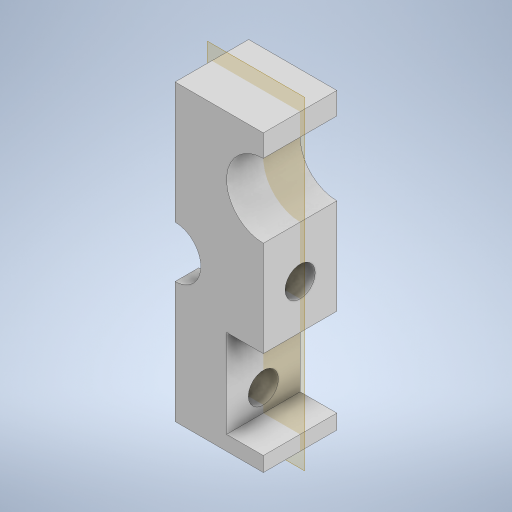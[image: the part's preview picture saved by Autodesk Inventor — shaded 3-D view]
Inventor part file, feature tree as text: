
AUTODESK INVENTOR PART (.ipt)
format: ipt  version: 2023 (Build 270158000, 158)  size: 332,288 bytes
history: native  units: mm
features: extrude x7, sketch x7, plane x1
ambient origin geometry x8: Origin, YZ Plane, XZ Plane, XY Plane, X Axis, Y Axis, Z Axis, Center Point
bodies: Solid1 (feature_tree)
feature tree (15):
  extrude  "Extrusion1"  Depth=20.0mm
  plane  "Work Plane1"
  extrude  "Extrusion2"  Depth=2.0mm
  extrude  "Extrusion3"  Depth=4.0mm
  extrude  "Extrusion4"  Depth=5.0mm TaperAngle=0.0deg
  extrude  "Extrusion5"  Depth=5.0mm TaperAngle=0.0deg
  extrude  "Extrusion6"  Depth=8.0mm TaperAngle=0.0deg
  extrude  "Extrusion7"  Depth=10.0mm
  sketch  "Sketch1"  dims[d0=20.0mm d1=20.0mm]
  sketch  "Sketch2"  dims[d2=4.0mm d6=2.0mm]
  sketch  "Sketch3"  dims[d7=2.0mm d8=4.0mm]
  sketch  "Sketch4"  dims[d9=2.0mm d10=5.0mm d11=0.0mm]
  sketch  "Sketch5"  dims[d12=5.0mm d13=1.8mm d14=0.0mm]
  sketch  "Sketch6"  dims[d15=3.5mm d16=8.0mm d17=0.0mm]
  sketch  "Sketch7"  dims[d18=2.05mm d19=2.05mm d20=2.5mm d21=2.5mm d22=2.5mm d23=2.5mm d24=5.0mm d25=0.0mm d30=5.0mm d31=0.0mm d32=2.5mm d33=1.0mm d34=6.0mm d35=5.0mm d36=4.0mm d37=5.0mm d38=0.0mm d39=2.5mm d40=10.0mm d41=2.05mm d42=12.0mm d43=0.0mm d44=6.0mm]
